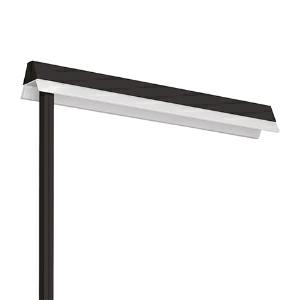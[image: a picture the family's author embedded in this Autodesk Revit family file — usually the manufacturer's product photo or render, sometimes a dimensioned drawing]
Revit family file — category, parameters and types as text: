
# Revit family: 3f_filippi_-_3f_mirella_floor_3f_filippi_-_12964_-_3f_mirella_floor_sf_bk_23_23_touch_dali_f5bc
name_source: partatom
category: Lighting Fixtures
units: mm (PartAtom-declared; Revit-internal decimal feet)

## family parameters
Cut with Voids When Loaded = No
Host = Face
Light Source = No
Part Type = Normal
Room Calculation Point = No
Round Connector Dimension = Use Diameter
Shared = No

## types (1)
- 3F Filippi - 3F Mirella Floor (1 x LED, 7042 lm, 52 W, 4000 K)
    Apparent Load = 52 VA
    Approval mark = ENEC
    CIE Flux Codes = 66 90 97 42 100
    Color Rendering = 80
    Color Temperature = 4000 K
    Control Gear = Electronic transformer
    Default Elevation = 1800 mm
    Description = ILLUMINOTECHNICAL
Luminous efficiency 100% (DLOR 42%, ULOR 58%).
Initial luminous flux of the luminaire 7042 lm.
Direct-indirect distribution.
Installation Interdistance Transv.D = 1.13 x hu - Long.D = 1.19 x hu.
Average luminance <3000 cd/m² for radial angles >65°.
Tabular UGR (CIE 117 - 4H-8H; S=0.25H; 70/50/20): RUG 13.5 - 15.7.
Beam angle: 80° - 88°.
Luminous efficacy 135 lm/W.
Lifetime (L93/B10): 30000 h. (tq+25°C)
Lifetime (L90/B10): 50000 h. (tq+25°C)
Lifetime (L85/B10): 80000 h. (tq+25°C)
Lifetime (L80/B10): 100000 h. (tq+25°C)
Sudden decreased luminous flux after 50000 hours: 0% (C0).
Photobiological safety in compliance with IEC/TR 62778: RG0 risk exempt, (IEC 62471).
In compliance with IEC/EN 62722-2-1 - IEC/EN 62717 standards.

SOURCE
2 linear LED modules 23W/840.
Energy efficiency class (UE 2019/2020 - UE 2019/2015): C.
CIE 13.3 Colour rendering index: CRI >80 (R9 <50%).
IES TM-30 Fidelity Index: Rf = 84 Rg = 95.
CCT nominal colour temperature 4000 K.
Colour initial tolerance (MacAdam): SDCM 3.

MECHANICAL
Housing in black painted extruded aluminium.
Heads in black painted zamak.
Pole in black painted stainless steel with a 30x30 mm square section fixed on a black painted steel base, dimensions 290x480 mm.
Methacrylate (PMMA) primary lens for total source shielding.
Anti-glare opal polycarbonate filter for brightness uniformity.
External lens of particular aesthetic value in satin methacrylate (PMMA).
Upper cover in transparent polycarbonate.
Luminaire with limited surface temperature. - D - (EN 60598-2-24)
Dimensions: 843x280 mm, height 2060 mm. Weight 15 kg.
IP40 protection degree.
Mechanical strength to impacts IK06 (1 joule).
Glow-wire test resistance 650°C.

ELECTRICAL
Halogen Free TOUCH DALI electronic wiring 230V-50/60Hz, power factor 0.95 at full load, THD <25%, constant output current, SELV, class I, 2 driver, 2 DALI addresses.
TOUCH DALI control integrated in the stem.
Power of the luminaire 52 W.
CE - IEC 60598-1 - EN 60598-1.
SAFE FLICKER: PstLM=<1 and SVM=<0.4 (IEC TR 61547-1 and IEC TR 63158), to ensure a more comfortable and safe light.
Ambient temperature from 0°C to +25°C.
Temperature class T6 max 85°C.
Relative humidity UR: <85%.

INSTALLATION
Floor.

SUPPLIED
Power supply with a 2.5 m long transparent cable, schuko plug.

APPLICATIONS
Free and flexible positioning for localized lighting on the workstation.
Environments where for technical reasons ceiling light points and environments with severe visual tasks cannot be equipped, where diffused and soft lighting is required for optimum visual comfort of the environment and total shielding of the source.
In environments with VDTs, managerial offices and staterooms.

LIGHT MANAGEMENT
Recommended minimum setting: 10%.
The TOUCH DALI control integrated in the stem, allows independent switching on, off and adjustment of the two emissions.

WARNING
Luminaire designed for disposal/recycling at end-of-life.
Replaceable (LED only) light source by a professional. Replaceable control gear by a professional.
    Height = 2060 mm
    Lamp = 1 x LED
    Lamp Light Flux = 7042 lm
    Lamp Power = 52 W
    Lamp count = 1
    Length = 843 mm
    Lifetime = 50000 h
    Luminous efficacy = 135 lm/W
    Manufacturer = 3F Filippi
    ModVariant = No
    Model = 3F Filippi - 12964 - 3F Mirella Floor SF BK 23+23 Touch DALI
    Mounting Place = Floor
    Mounting Type = Surface mounted
    Number of Poles = 1
    OnlyDefault = Yes
    Power Factor = 1
    Product Name = 3F Filippi - 3F Mirella Floor
    Product group = freestanding uplighter
    ProductGroupID = 1310
    Protection Class = Protection class I
    Protection Degree = IP 40
    RLX_Detail_Level = 1
    RLX_Emergency_Light_Flux = 0 lm
    RLX_Emergency_Type = 0
    RLX_Emergency_Type_DB = No
    RlxData = <blob elided: 99217 chars, md5=349495d9>
    Socket = socket
    Standby Power = 0 W
    System Light Flux = 7042 lm
    System Power = 52 W
    Type Comments = Product without accessories
    Type Image = 3ffilippi_3f_mirella_floor_bk.jpg
    URL = http://relux.com
    VarID = ---
    Voltage = 0 V
    Weight = 0.00 kg
    Width = 280 mm

## geometry (parser evidence)
native form markers: Blend x4, Sweep x12
no freeform markers — native parametric forms only
